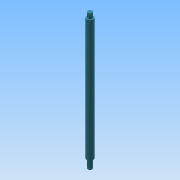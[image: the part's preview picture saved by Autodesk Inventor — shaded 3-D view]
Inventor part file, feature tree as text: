
AUTODESK INVENTOR PART (.ipt)
format: ipt  version: 2015 (Build 190159000, 159)  size: 141,824 bytes
history: native  units: mm
features: sketch x7, extrude x5, revolve x2, chamfer x2, plane x1
ambient origin geometry x8: Origin, YZ Plane, XZ Plane, XY Plane, X Axis, Y Axis, Z Axis, Center Point
bodies: 实体1 (feature_tree)
feature tree (17):
  extrude  "拉伸1"  Depth=561.864mm TaperAngle=0.0deg
  extrude  "拉伸2"  Depth=23.97mm TaperAngle=0.0deg
  plane  "工作平面1"
  extrude  "拉伸3"  Depth=6.0mm
  revolve  "旋转1"  [1 undecoded]
  chamfer  "倒角1"  Distance=2.5mm
  extrude  "拉伸4"  Depth=9.175mm
  extrude  "拉伸5"  Depth=4.0mm
  revolve  "旋转2"  Angle=90.0deg
  chamfer  "倒角2"  Distance=0.5mm Angle=45.0deg
  sketch  "草图1"  dims[d0=30.0mm d1=561.864mm d2=0.0mm]
  sketch  "草图2"  dims[d3=20.0mm d4=23.97mm d5=0.0mm]
  sketch  "草图3"  dims[d6=30.507477mm d7=6.0mm]
  sketch  "草图4"  dims[d8=8.0mm d9=5.385mm d10=2.5mm d11=0.0mm]
  sketch  "草图5"  dims[d12=472.235217mm d13=9.175mm]
  sketch  "草图6"  dims[d14=1.2mm d15=4.0mm]
  sketch  "草图7"  dims[d16=2.117493mm d17=90.0deg d18=0.5mm d19=2.0mm d20=45.0deg d21=20.0mm d22=41.61mm d23=0.0mm d24=6.0mm d25=26.0mm d26=5.205mm d27=2.5mm d28=0.0mm d29=4.299985mm d30=1.2mm d31=5.81217mm d32=4.0mm d33=9.175mm d34=90.0deg d35=1.0mm d36=2.0mm d37=45.0deg]
note: 1 required parameter value undecoded (feature->parameter linkage not recoverable at this tier; creation-order binding heuristic only, values carry confidence <= 0.55)
